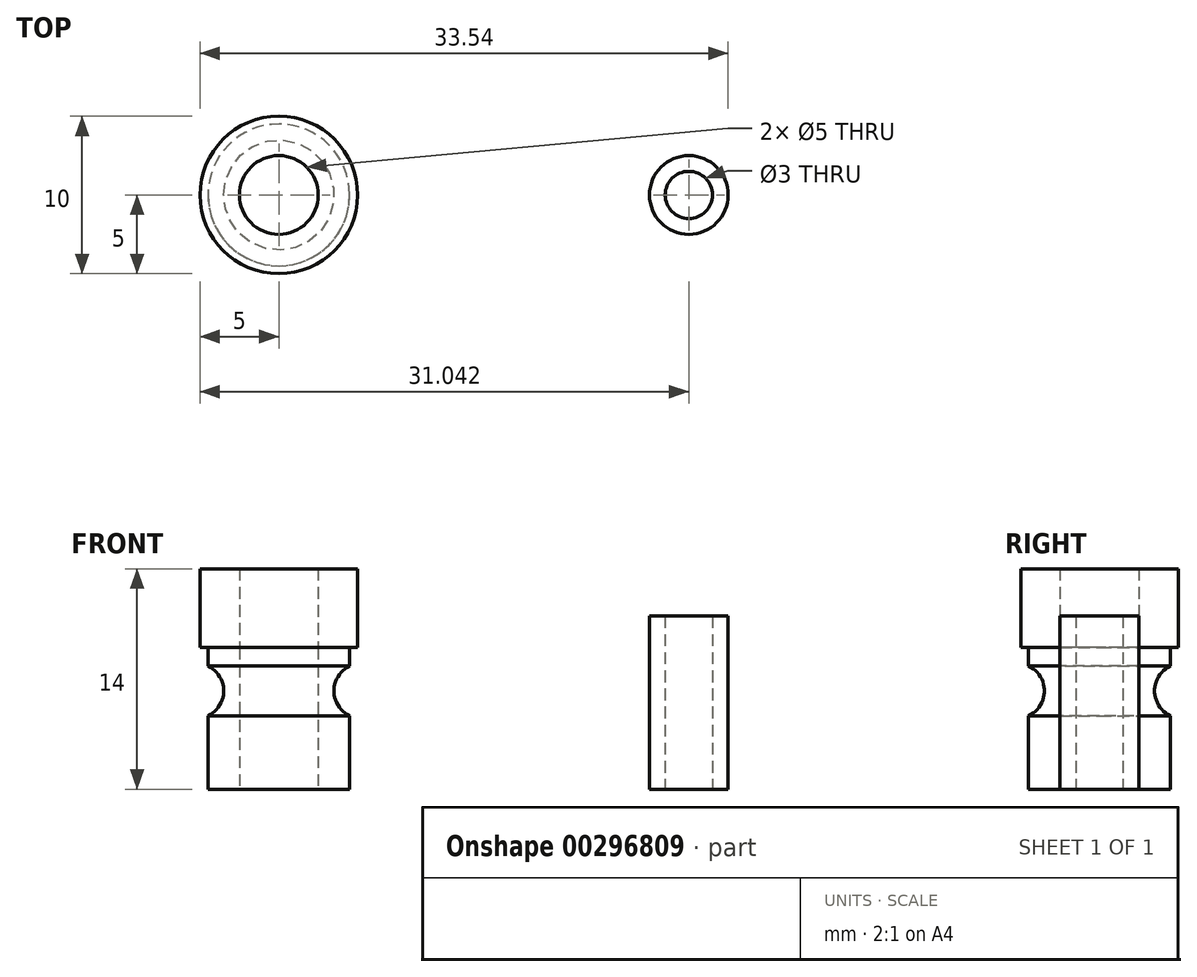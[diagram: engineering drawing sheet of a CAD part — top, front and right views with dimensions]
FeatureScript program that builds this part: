
annotation { "Feature Type Name" : "Feature", "Feature Type Description" : "" }
export const myFeature = defineFeature(function(context is Context, id is Id, definition is map)
    precondition{}
    {
        {
            assignVariable(context, id + "F0", {"name" : "Diameter", "anyValue" : 9});
        }
        {
            var Q0;
            Q0=qCreatedBy(makeId("Top.planeOp"),FACE);
            var sketch = newSketch(context, id + "F1", { "sketchPlane" : qUnion([Q0])});
            skCircle(sketch, "E0", {"center": v(0, 0) * mm, "radius": 4.5 * mm});
            skCircle(sketch, "E1", {"center": v(0, 0) * mm, "radius": 2.5 * mm});
            skSolve(sketch);
        }
        {
            var Q0;
            Q0=makeQuery(id+"F1.imprint","IMPRINT",FACE,{"disambiguationData":[TD([[makeQuery(id+"F1.imprint","IMPRINT",EDGE,{"derivedFrom":sQuery(id+"F1.wireOp",EDGE,"E0")}),1.0]])]});
            extrude(context, id + "F2", {"entities" : qUnion([Q0]), "depth" : (getVariable(context, 'Diameter')) * mm});
        }
        {
            var Q0;
            Q0=qCreatedBy(makeId("Front.planeOp"),FACE);
            var sketch = newSketch(context, id + "F3", { "sketchPlane" : qUnion([Q0])});
            skCircle(sketch, "E2", {"center": v(-5.25, 6.25) * mm, "radius": 1.75 * mm});
            skCircle(sketch, "E3", {"center": v(0, 6.25) * mm, "radius": 4.5 * mm, "construction": true});
            skSolve(sketch);
        }
        {
            var Q0;
            Q0=makeQuery(id+"F3.imprint","IMPRINT",FACE,{"disambiguationData":[TD([[makeQuery(id+"F3.imprint","IMPRINT",EDGE,{"derivedFrom":sQuery(id+"F3.wireOp",EDGE,"E2")}),1.0]])]});
            var Q1;
            Q1=makeQuery(id+"F2.opExtrude","SWEPT_FACE",FACE,{"disambiguationData":[OSD([sQuery(id+"F1.wireOp",EDGE,"E0")])]});
            revolve(context, id + "F4", {"operationType" : NewBodyOperationType.REMOVE, "entities" : qUnion([Q0]), "axis" : qUnion([Q1]), "revolveType" : RevolveType.FULL, "oppositeDirection" : true});
        }
        {
            var Q0;
            Q0=makeQuery(id+"F2.opExtrude","CAP_FACE",FACE,{"disambiguationData":[OSD([sQuery(id+"F1.wireOp",EDGE,"E0"),sQuery(id+"F1.wireOp",EDGE,"E1")])],"isStart":false});
            var sketch = newSketch(context, id + "F5", { "sketchPlane" : qUnion([Q0])});
            skCircle(sketch, "E4", {"center": v(0, 0) * mm, "radius": 5 * mm});
            skCircle(sketch, "E5", {"center": v(0, 0) * mm, "radius": 1.5 * mm});
            skSolve(sketch);
        }
        {
            var Q0;
            Q0=makeQuery(id+"F5.imprint","IMPRINT",FACE,{"disambiguationData":[TD([[makeQuery(id+"F5.imprint","IMPRINT",EDGE,{"derivedFrom":sQuery(id+"F5.wireOp",EDGE,"E4")}),1.0]])]});
            var Q1;
            Q1=makeQuery(id+"F5.imprint","IMPRINT",FACE,{"disambiguationData":[TD([[makeQuery(id+"F5.imprint","IMPRINT",EDGE,{"derivedFrom":makeQuery(id+"F2.opExtrude","CAP_EDGE",EDGE,{"disambiguationData":[OSD([sQuery(id+"F1.wireOp",EDGE,"E0")])],"isStart":false})}),1.0]])]});
            extrude(context, id + "F6", {"entities" : qUnion([Q0, Q1]), "depth" : 5 * mm});
        }
        {
            var Q0;
            Q0=qCreatedBy(makeId("Top.planeOp"),FACE);
            var sketch = newSketch(context, id + "F7", { "sketchPlane" : qUnion([Q0])});
            skCircle(sketch, "E6", {"center": v(26.04, 0) * mm, "radius": 2.5 * mm});
            skCircle(sketch, "E7", {"center": v(26.04, 0) * mm, "radius": 1.5 * mm});
            skSolve(sketch);
        }
        {
            var Q0;
            Q0=makeQuery(id+"F7.imprint","IMPRINT",FACE,{"disambiguationData":[TD([[makeQuery(id+"F7.imprint","IMPRINT",EDGE,{"derivedFrom":sQuery(id+"F7.wireOp",EDGE,"E6")}),1.0]])]});
            extrude(context, id + "F8", {"entities" : qUnion([Q0]), "depth" : 11 * mm, "offsetDistance" : 25 * mm});
        }
    });
